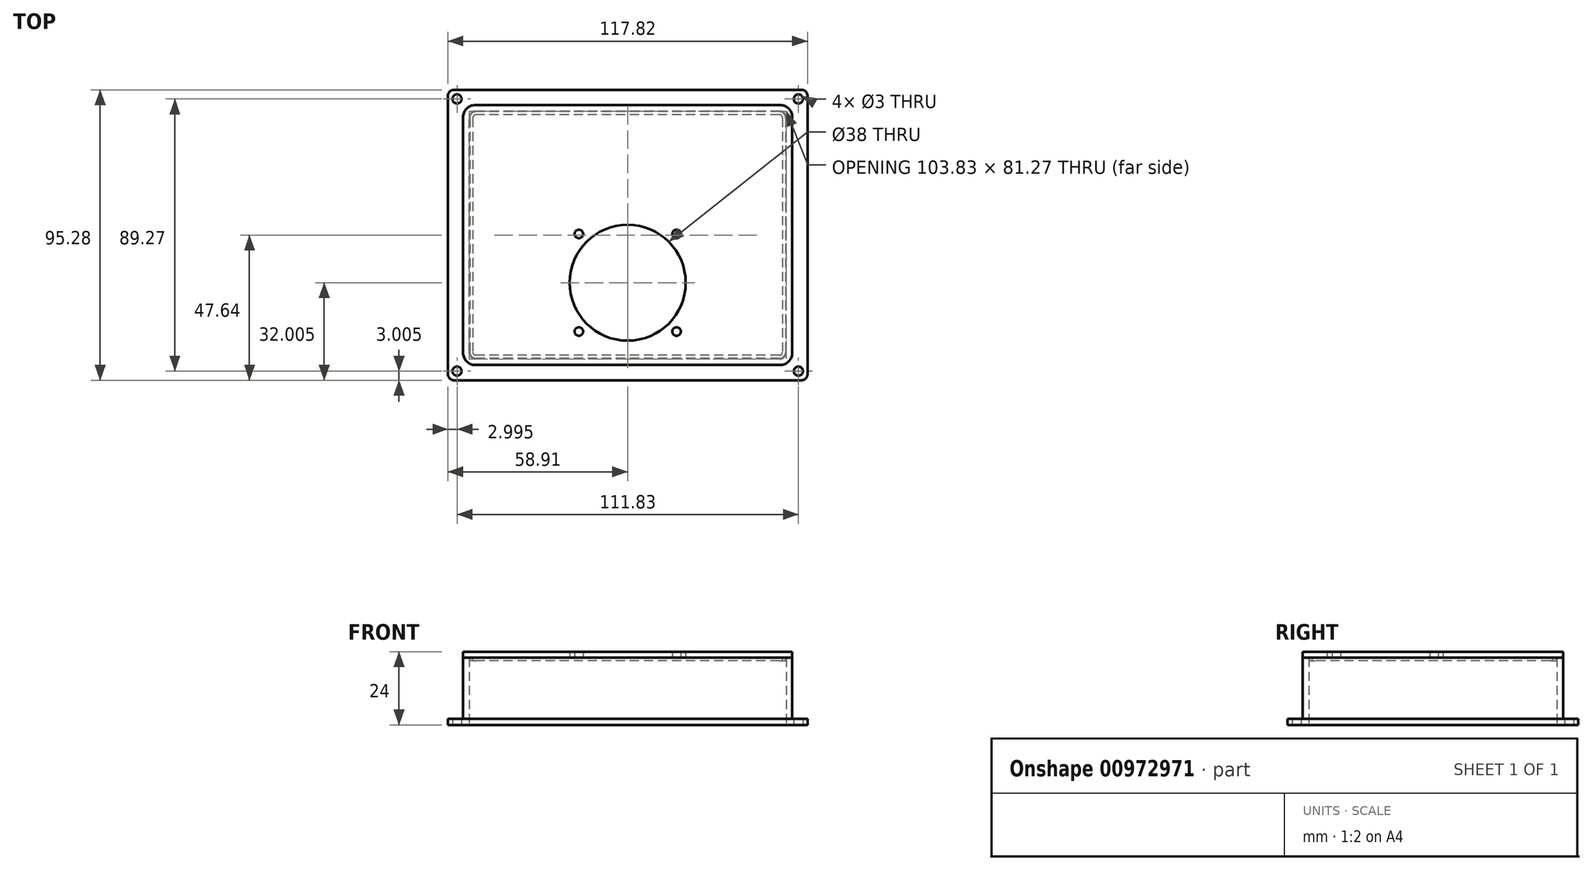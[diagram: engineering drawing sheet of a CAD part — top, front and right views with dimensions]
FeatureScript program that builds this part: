
annotation { "Feature Type Name" : "Feature", "Feature Type Description" : "" }
export const myFeature = defineFeature(function(context is Context, id is Id, definition is map)
    precondition{}
    {
        {
            var Q0;
            Q0=qCreatedBy(makeId("Top.planeOp"),FACE);
            var sketch = newSketch(context, id + "F0", { "sketchPlane" : qUnion([Q0])});
            skLineSegment(sketch, "E0.bottom", {"start": v(58.92, -47.64) * mm, "end": v(-58.91, -47.64) * mm});
            skLineSegment(sketch, "E0.top", {"start": v(58.92, 47.63) * mm, "end": v(-58.91, 47.63) * mm});
            skLineSegment(sketch, "E0.left", {"start": v(58.92, -47.64) * mm, "end": v(58.92, 47.63) * mm});
            skLineSegment(sketch, "E0.right", {"start": v(-58.91, -47.64) * mm, "end": v(-58.91, 47.63) * mm});
            skPoint(sketch, "E0.middle", {"position": v(0, 0) * mm});
            skLineSegment(sketch, "E1.bottom", {"start": v(51.92, -40.64) * mm, "end": v(-51.92, -40.64) * mm});
            skLineSegment(sketch, "E1.top", {"start": v(51.92, 40.64) * mm, "end": v(-51.92, 40.64) * mm});
            skLineSegment(sketch, "E1.left", {"start": v(51.92, -40.64) * mm, "end": v(51.92, 40.64) * mm});
            skLineSegment(sketch, "E1.right", {"start": v(-51.92, -40.64) * mm, "end": v(-51.92, 40.64) * mm});
            skLineSegment(sketch, "E2.bottom", {"start": v(55.92, -44.63) * mm, "end": v(-55.91, -44.64) * mm, "construction": true});
            skLineSegment(sketch, "E2.top", {"start": v(55.91, 44.64) * mm, "end": v(-55.92, 44.63) * mm, "construction": true});
            skLineSegment(sketch, "E2.left", {"start": v(55.92, -44.63) * mm, "end": v(55.91, 44.64) * mm, "construction": true});
            skLineSegment(sketch, "E2.right", {"start": v(-55.91, -44.64) * mm, "end": v(-55.92, 44.63) * mm, "construction": true});
            skCircle(sketch, "E3", {"center": v(-55.92, 44.63) * mm, "radius": 1.5 * mm});
            skCircle(sketch, "E4", {"center": v(55.91, 44.64) * mm, "radius": 1.5 * mm});
            skCircle(sketch, "E5", {"center": v(55.92, -44.63) * mm, "radius": 1.5 * mm});
            skCircle(sketch, "E6", {"center": v(-55.91, -44.64) * mm, "radius": 1.5 * mm});
            skSolve(sketch);
        }
        {
            var Q0;
            Q0 = qSketchRegion(id + "F0", true);
            extrude(context, id + "F1", {"entities" : qUnion([Q0]), "depth" : 2 * mm, "offsetDistance" : 25 * mm});
        }
        {
            var Q0;
            Q0=makeQuery(id+"F1.opExtrude","CAP_FACE",FACE,{"disambiguationData":[OSD([sQuery(id+"F0.wireOp",EDGE,"E0.bottom"),sQuery(id+"F0.wireOp",EDGE,"E0.top"),sQuery(id+"F0.wireOp",EDGE,"E0.left"),sQuery(id+"F0.wireOp",EDGE,"E0.right"),sQuery(id+"F0.wireOp",EDGE,"E1.bottom"),sQuery(id+"F0.wireOp",EDGE,"E1.top"),sQuery(id+"F0.wireOp",EDGE,"E1.left"),sQuery(id+"F0.wireOp",EDGE,"E1.right"),sQuery(id+"F0.wireOp",EDGE,"E3"),sQuery(id+"F0.wireOp",EDGE,"E4"),sQuery(id+"F0.wireOp",EDGE,"E5"),sQuery(id+"F0.wireOp",EDGE,"E6")])],"isStart":false});
            var sketch = newSketch(context, id + "F2", { "sketchPlane" : qUnion([Q0])});
            skLineSegment(sketch, "E7.bottom", {"start": v(51.92, -40.64) * mm, "end": v(-51.92, -40.64) * mm});
            skLineSegment(sketch, "E7.top", {"start": v(51.92, 40.64) * mm, "end": v(-51.92, 40.64) * mm});
            skLineSegment(sketch, "E7.left", {"start": v(51.92, -40.64) * mm, "end": v(51.92, 40.64) * mm});
            skLineSegment(sketch, "E7.right", {"start": v(-51.92, -40.64) * mm, "end": v(-51.92, 40.64) * mm});
            skPoint(sketch, "E7.middle", {"position": v(0, 0) * mm});
            skLineSegment(sketch, "E8.bottom", {"start": v(53.91, -42.63) * mm, "end": v(-53.91, -42.63) * mm});
            skLineSegment(sketch, "E8.top", {"start": v(53.91, 42.63) * mm, "end": v(-53.91, 42.63) * mm});
            skLineSegment(sketch, "E8.left", {"start": v(53.91, -42.63) * mm, "end": v(53.91, 42.63) * mm});
            skLineSegment(sketch, "E8.right", {"start": v(-53.91, -42.63) * mm, "end": v(-53.91, 42.63) * mm});
            skSolve(sketch);
        }
        {
            var Q0;
            Q0 = qSketchRegion(id + "F2", true);
            extrude(context, id + "F3", {"entities" : qUnion([Q0]), "operationType" : NewBodyOperationType.ADD, "depth" : 20 * mm, "offsetDistance" : 25 * mm});
        }
        {
            var Q0;
            Q0=makeQuery(id+"F1.opExtrude","SWEPT_EDGE",EDGE,{"disambiguationData":[OSD([sQuery(id+"F0.wireOp",EDGE,"E0.bottom"),sQuery(id+"F0.wireOp",EDGE,"E0.right")])]});
            var Q1;
            Q1=makeQuery(id+"F1.opExtrude","SWEPT_EDGE",EDGE,{"disambiguationData":[OSD([sQuery(id+"F0.wireOp",EDGE,"E0.bottom"),sQuery(id+"F0.wireOp",EDGE,"E0.left")])]});
            var Q2;
            Q2=makeQuery(id+"F1.opExtrude","SWEPT_EDGE",EDGE,{"disambiguationData":[OSD([sQuery(id+"F0.wireOp",EDGE,"E0.top"),sQuery(id+"F0.wireOp",EDGE,"E0.right")])]});
            var Q3;
            Q3=makeQuery(id+"F1.opExtrude","SWEPT_EDGE",EDGE,{"disambiguationData":[OSD([sQuery(id+"F0.wireOp",EDGE,"E0.top"),sQuery(id+"F0.wireOp",EDGE,"E0.left")])]});
            fillet(context, id + "F4", {"entities" : qUnion([Q0, Q1, Q2, Q3]), "radius" : 2 * mm, "tangentPropagation" : true, "allowEdgeOverflow" : false});
        }
        {
            var Q0;
            Q0=makeQuery(id+"F3.opExtrude","CAP_FACE",FACE,{"disambiguationData":[OSD([sQuery(id+"F2.wireOp",EDGE,"E7.bottom"),sQuery(id+"F2.wireOp",EDGE,"E7.top"),sQuery(id+"F2.wireOp",EDGE,"E7.left"),sQuery(id+"F2.wireOp",EDGE,"E7.right"),sQuery(id+"F2.wireOp",EDGE,"E8.bottom"),sQuery(id+"F2.wireOp",EDGE,"E8.top"),sQuery(id+"F2.wireOp",EDGE,"E8.left"),sQuery(id+"F2.wireOp",EDGE,"E8.right")])],"isStart":false});
            var sketch = newSketch(context, id + "F5", { "sketchPlane" : qUnion([Q0])});
            skLineSegment(sketch, "E9.bottom", {"start": v(-53.91, 42.63) * mm, "end": v(53.91, 42.63) * mm});
            skLineSegment(sketch, "E9.top", {"start": v(-53.91, -42.63) * mm, "end": v(53.91, -42.63) * mm});
            skLineSegment(sketch, "E9.left", {"start": v(-53.91, 42.63) * mm, "end": v(-53.91, -42.63) * mm});
            skLineSegment(sketch, "E9.right", {"start": v(53.91, 42.63) * mm, "end": v(53.91, -42.63) * mm});
            skPoint(sketch, "E9.middle", {"position": v(0, 0) * mm});
            skPoint(sketch, "E10", {"position": v(0, -15.64) * mm});
            skCircle(sketch, "E11", {"center": v(0, -15.64) * mm, "radius": 19 * mm});
            skLineSegment(sketch, "E12.bottom", {"start": v(16, -31.63) * mm, "end": v(-16, -31.63) * mm, "construction": true});
            skLineSegment(sketch, "E12.top", {"start": v(16, 0.36) * mm, "end": v(-16, 0.36) * mm, "construction": true});
            skLineSegment(sketch, "E12.left", {"start": v(16, -31.63) * mm, "end": v(16, 0.36) * mm, "construction": true});
            skLineSegment(sketch, "E12.right", {"start": v(-16, -31.63) * mm, "end": v(-16, 0.36) * mm, "construction": true});
            skCircle(sketch, "E13", {"center": v(-16, 0.36) * mm, "radius": 1.4 * mm});
            skCircle(sketch, "E14", {"center": v(16, 0.36) * mm, "radius": 1.4 * mm});
            skCircle(sketch, "E15", {"center": v(-16, -31.63) * mm, "radius": 1.4 * mm});
            skCircle(sketch, "E16", {"center": v(16, -31.63) * mm, "radius": 1.4 * mm});
            skSolve(sketch);
        }
        {
            var Q0;
            Q0 = qSketchRegion(id + "F5", true);
            extrude(context, id + "F6", {"entities" : qUnion([Q0]), "depth" : 2 * mm, "offsetDistance" : 25 * mm});
        }
        {
            var Q0;
            Q0=makeQuery(id+"F6.opExtrude","CAP_FACE",FACE,{"disambiguationData":[OSD([sQuery(id+"F5.wireOp",EDGE,"E9.bottom"),sQuery(id+"F5.wireOp",EDGE,"E9.top"),sQuery(id+"F5.wireOp",EDGE,"E9.left"),sQuery(id+"F5.wireOp",EDGE,"E9.right"),sQuery(id+"F5.wireOp",EDGE,"E11"),sQuery(id+"F5.wireOp",EDGE,"E13"),sQuery(id+"F5.wireOp",EDGE,"E14"),sQuery(id+"F5.wireOp",EDGE,"E15"),sQuery(id+"F5.wireOp",EDGE,"E16")])],"isStart":true});
            var sketch = newSketch(context, id + "F7", { "sketchPlane" : qUnion([Q0])});
            skLineSegment(sketch, "E17.bottom", {"start": v(51.71, -40.44) * mm, "end": v(-51.71, -40.44) * mm});
            skLineSegment(sketch, "E17.top", {"start": v(51.71, 40.44) * mm, "end": v(-51.71, 40.44) * mm});
            skLineSegment(sketch, "E17.left", {"start": v(51.71, -40.44) * mm, "end": v(51.71, 40.44) * mm});
            skLineSegment(sketch, "E17.right", {"start": v(-51.71, -40.44) * mm, "end": v(-51.71, 40.44) * mm});
            skPoint(sketch, "E17.middle", {"position": v(0, 0) * mm});
            skLineSegment(sketch, "E18.bottom", {"start": v(50.72, -39.44) * mm, "end": v(-50.72, -39.44) * mm});
            skLineSegment(sketch, "E18.top", {"start": v(50.72, 39.44) * mm, "end": v(-50.72, 39.44) * mm});
            skLineSegment(sketch, "E18.left", {"start": v(50.72, -39.44) * mm, "end": v(50.72, 39.44) * mm});
            skLineSegment(sketch, "E18.right", {"start": v(-50.72, -39.44) * mm, "end": v(-50.72, 39.44) * mm});
            skSolve(sketch);
        }
        {
            var Q0;
            Q0 = qSketchRegion(id + "F7", true);
            extrude(context, id + "F8", {"entities" : qUnion([Q0]), "operationType" : NewBodyOperationType.ADD, "depth" : 1 * mm, "offsetDistance" : 25 * mm});
        }
        {
            var Q0;
            Q0=makeQuery(id+"F3.boolean.opBoolean","MERGE",EDGE,{"derivedFrom":[makeQuery(id+"F1.opExtrude","SWEPT_EDGE",EDGE,{"disambiguationData":[OSD([sQuery(id+"F0.wireOp",EDGE,"E1.top"),sQuery(id+"F0.wireOp",EDGE,"E1.left")])]}),makeQuery(id+"F3.opExtrude","SWEPT_EDGE",EDGE,{"disambiguationData":[OSD([sQuery(id+"F2.wireOp",EDGE,"E7.top"),sQuery(id+"F2.wireOp",EDGE,"E7.left")])]})]});
            var Q1;
            Q1=makeQuery(id+"F3.boolean.opBoolean","MERGE",EDGE,{"derivedFrom":[makeQuery(id+"F1.opExtrude","SWEPT_EDGE",EDGE,{"disambiguationData":[OSD([sQuery(id+"F0.wireOp",EDGE,"E1.bottom"),sQuery(id+"F0.wireOp",EDGE,"E1.left")])]}),makeQuery(id+"F3.opExtrude","SWEPT_EDGE",EDGE,{"disambiguationData":[OSD([sQuery(id+"F2.wireOp",EDGE,"E7.bottom"),sQuery(id+"F2.wireOp",EDGE,"E7.left")])]})]});
            var Q2;
            Q2=makeQuery(id+"F3.boolean.opBoolean","MERGE",EDGE,{"derivedFrom":[makeQuery(id+"F1.opExtrude","SWEPT_EDGE",EDGE,{"disambiguationData":[OSD([sQuery(id+"F0.wireOp",EDGE,"E1.bottom"),sQuery(id+"F0.wireOp",EDGE,"E1.right")])]}),makeQuery(id+"F3.opExtrude","SWEPT_EDGE",EDGE,{"disambiguationData":[OSD([sQuery(id+"F2.wireOp",EDGE,"E7.bottom"),sQuery(id+"F2.wireOp",EDGE,"E7.right")])]})]});
            var Q3;
            Q3=makeQuery(id+"F3.boolean.opBoolean","MERGE",EDGE,{"derivedFrom":[makeQuery(id+"F1.opExtrude","SWEPT_EDGE",EDGE,{"disambiguationData":[OSD([sQuery(id+"F0.wireOp",EDGE,"E1.top"),sQuery(id+"F0.wireOp",EDGE,"E1.right")])]}),makeQuery(id+"F3.opExtrude","SWEPT_EDGE",EDGE,{"disambiguationData":[OSD([sQuery(id+"F2.wireOp",EDGE,"E7.top"),sQuery(id+"F2.wireOp",EDGE,"E7.right")])]})]});
            var Q4;
            Q4=makeQuery(id+"F8.opExtrude","SWEPT_EDGE",EDGE,{"disambiguationData":[OSD([sQuery(id+"F7.wireOp",EDGE,"E17.top"),sQuery(id+"F7.wireOp",EDGE,"E17.left")])]});
            var Q5;
            Q5=makeQuery(id+"F8.opExtrude","SWEPT_EDGE",EDGE,{"disambiguationData":[OSD([sQuery(id+"F7.wireOp",EDGE,"E17.bottom"),sQuery(id+"F7.wireOp",EDGE,"E17.left")])]});
            var Q6;
            Q6=makeQuery(id+"F8.opExtrude","SWEPT_EDGE",EDGE,{"disambiguationData":[OSD([sQuery(id+"F7.wireOp",EDGE,"E17.bottom"),sQuery(id+"F7.wireOp",EDGE,"E17.right")])]});
            var Q7;
            Q7=makeQuery(id+"F8.opExtrude","SWEPT_EDGE",EDGE,{"disambiguationData":[OSD([sQuery(id+"F7.wireOp",EDGE,"E17.top"),sQuery(id+"F7.wireOp",EDGE,"E17.right")])]});
            fillet(context, id + "F9", {"entities" : qUnion([Q0, Q1, Q2, Q3, Q4, Q5, Q6, Q7]), "radius" : 2 * mm, "tangentPropagation" : true, "allowEdgeOverflow" : false});
        }
        {
            var Q0;
            Q0=makeQuery(id+"F8.opExtrude","SWEPT_EDGE",EDGE,{"disambiguationData":[OSD([sQuery(id+"F7.wireOp",EDGE,"E18.top"),sQuery(id+"F7.wireOp",EDGE,"E18.right")])]});
            var Q1;
            Q1=makeQuery(id+"F8.opExtrude","SWEPT_EDGE",EDGE,{"disambiguationData":[OSD([sQuery(id+"F7.wireOp",EDGE,"E18.top"),sQuery(id+"F7.wireOp",EDGE,"E18.left")])]});
            var Q2;
            Q2=makeQuery(id+"F8.opExtrude","SWEPT_EDGE",EDGE,{"disambiguationData":[OSD([sQuery(id+"F7.wireOp",EDGE,"E18.bottom"),sQuery(id+"F7.wireOp",EDGE,"E18.right")])]});
            var Q3;
            Q3=makeQuery(id+"F8.opExtrude","SWEPT_EDGE",EDGE,{"disambiguationData":[OSD([sQuery(id+"F7.wireOp",EDGE,"E18.bottom"),sQuery(id+"F7.wireOp",EDGE,"E18.left")])]});
            fillet(context, id + "F10", {"entities" : qUnion([Q0, Q1, Q2, Q3]), "radius" : 1 * mm, "tangentPropagation" : true, "allowEdgeOverflow" : false});
        }
        {
            var Q0;
            Q0=makeQuery(id+"F3.opExtrude","SWEPT_EDGE",EDGE,{"disambiguationData":[OSD([sQuery(id+"F2.wireOp",EDGE,"E8.bottom"),sQuery(id+"F2.wireOp",EDGE,"E8.left")])]});
            var Q1;
            Q1=makeQuery(id+"F3.opExtrude","SWEPT_EDGE",EDGE,{"disambiguationData":[OSD([sQuery(id+"F2.wireOp",EDGE,"E8.bottom"),sQuery(id+"F2.wireOp",EDGE,"E8.right")])]});
            var Q2;
            Q2=makeQuery(id+"F3.opExtrude","SWEPT_EDGE",EDGE,{"disambiguationData":[OSD([sQuery(id+"F2.wireOp",EDGE,"E8.top"),sQuery(id+"F2.wireOp",EDGE,"E8.right")])]});
            var Q3;
            Q3=makeQuery(id+"F3.opExtrude","SWEPT_EDGE",EDGE,{"disambiguationData":[OSD([sQuery(id+"F2.wireOp",EDGE,"E8.top"),sQuery(id+"F2.wireOp",EDGE,"E8.left")])]});
            var Q4;
            Q4=makeQuery(id+"F6.opExtrude","SWEPT_EDGE",EDGE,{"disambiguationData":[OSD([sQuery(id+"F5.wireOp",EDGE,"E9.bottom"),sQuery(id+"F5.wireOp",EDGE,"E9.right")])]});
            var Q5;
            Q5=makeQuery(id+"F6.opExtrude","SWEPT_EDGE",EDGE,{"disambiguationData":[OSD([sQuery(id+"F5.wireOp",EDGE,"E9.bottom"),sQuery(id+"F5.wireOp",EDGE,"E9.left")])]});
            var Q6;
            Q6=makeQuery(id+"F6.opExtrude","SWEPT_EDGE",EDGE,{"disambiguationData":[OSD([sQuery(id+"F5.wireOp",EDGE,"E9.top"),sQuery(id+"F5.wireOp",EDGE,"E9.left")])]});
            var Q7;
            Q7=makeQuery(id+"F6.opExtrude","SWEPT_EDGE",EDGE,{"disambiguationData":[OSD([sQuery(id+"F5.wireOp",EDGE,"E9.top"),sQuery(id+"F5.wireOp",EDGE,"E9.right")])]});
            fillet(context, id + "F11", {"entities" : qUnion([Q0, Q1, Q2, Q3, Q4, Q5, Q6, Q7]), "radius" : 4 * mm, "tangentPropagation" : true, "allowEdgeOverflow" : false});
        }
    });
